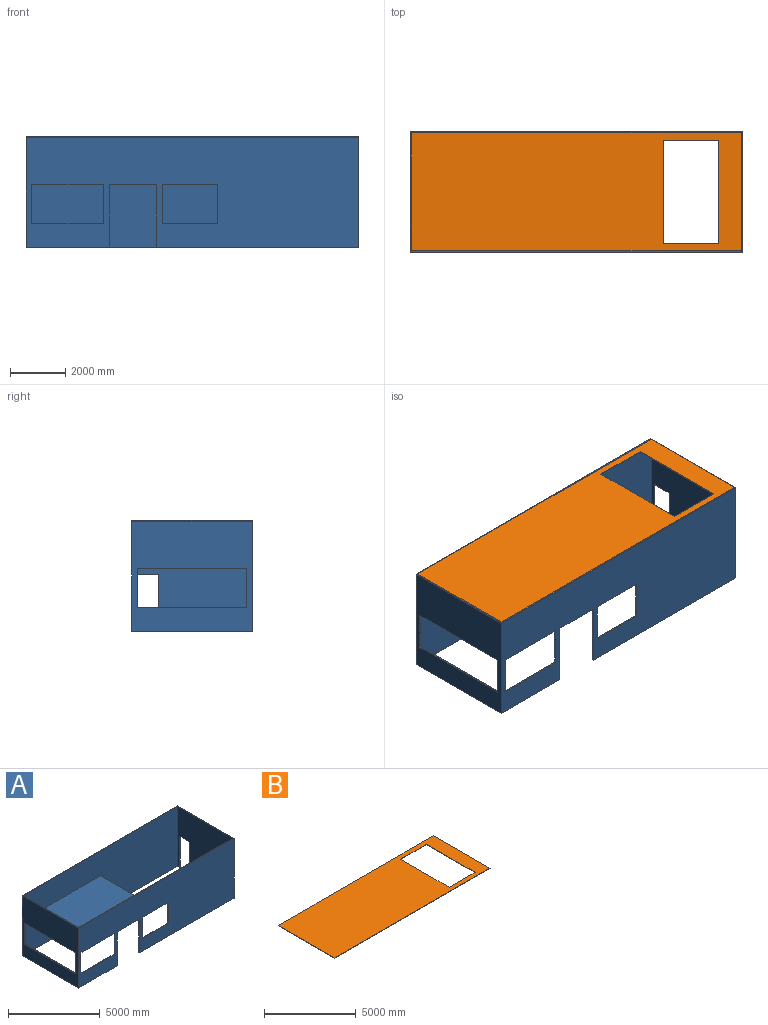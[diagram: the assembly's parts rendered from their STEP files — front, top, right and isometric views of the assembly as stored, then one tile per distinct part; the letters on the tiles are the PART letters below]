
ASSEMBLY  parts=2 mates=1
PART A: 33 faces, bbox 12000x4350x4000 mm
  f0: plane 11925x4000mm, normal (0,1,0), area 36997700mm2, adj f2,f3,f4,f5,f6,f7,f8,f9
  f1: plane 11925x4000mm, normal (0,-1,0), area 47402500mm2, adj f2,f3,f10,f12,f26,f27,f28,f29
  f2: plane 4260x2300mm, normal (1,0,0), area 4208750mm2, adj f0,f1,f10,f21,f22,f23,f25,f28
  f3: plane 4260x1650mm, normal (1,0,0), area 7029000mm2, adj f0,f1,f12,f27
  f4: plane 2600x50mm, normal (0,0,-1), area 130000mm2, adj f0,f5,f19,f20
  f5: plane 1415x50mm, normal (1,0,0), area 70750mm2, adj f0,f4,f6,f20
  f6: plane 2600x50mm, normal (0,0,1), area 130000mm2, adj f0,f5,f19,f20
  f7: plane 2000x50mm, normal (0,0,-1), area 100000mm2, adj f0,f8,f17,f20
  f8: plane 1415x50mm, normal (1,0,0), area 70750mm2, adj f0,f7,f9,f20
  f9: plane 2000x50mm, normal (0,0,1), area 100000mm2, adj f0,f8,f17,f20
  f10: plane 12000x4350mm, normal (0,0,-1), area 847000mm2, adj f0,f1,f2,f11,f13,f18,f20,f24
  f11: plane 4350x4000mm, normal (-1,0,0), area 11810750mm2, adj f10,f12,f20,f21,f22,f23,f24,f25
  f12: plane 12000x4350mm, normal (0,0,1), area 1399500mm2, adj f0,f1,f3,f11,f13,f20,f24,f29
  f13: plane 4350x4000mm, normal (1,0,0), area 15826800mm2, adj f10,f12,f14,f20,f24,f30,f31,f32
  f14: plane 7280x3390mm, normal (0,0,-1), area 447500mm2, adj f0,f13,f15,f20,f29,f30
  f15: plane 2265x50mm, normal (-1,0,0), area 113250mm2, adj f0,f14,f16,f20
  f16: plane 1720x50mm, normal (0,0,-1), area 86000mm2, adj f0,f15,f18,f20
  f17: plane 1415x50mm, normal (-1,0,0), area 70750mm2, adj f0,f7,f9,f20
  f18: plane 2265x50mm, normal (1,0,0), area 113250mm2, adj f0,f10,f16,f20
  f19: plane 1415x50mm, normal (-1,0,0), area 70750mm2, adj f0,f4,f6,f20
  f20: plane 12000x4000mm, normal (0,-1,0), area 37595200mm2, adj f4,f5,f6,f7,f8,f9,f10,f11
  f21: plane 3950x50mm, normal (0,0,-1), area 197500mm2, adj f2,f11,f22,f25
  f22: plane 1415x50mm, normal (0,-1,0), area 70750mm2, adj f2,f11,f21,f23
  f23: plane 3950x50mm, normal (0,0,1), area 197500mm2, adj f2,f11,f22,f25
  f24: plane 12000x4000mm, normal (0,1,0), area 48000000mm2, adj f10,f11,f12,f13
  f25: plane 1415x50mm, normal (0,1,0), area 70750mm2, adj f2,f11,f21,f23
  f26: plane 4260x50mm, normal (1,0,0), area 213000mm2, adj f0,f1,f27,f28
  f27: plane 5950x4260mm, normal (0,0,1), area 25347000mm2, adj f0,f1,f3,f26
  f28: plane 5950x4260mm, normal (0,0,-1), area 25347000mm2, adj f0,f1,f2,f26
  f29: plane 4260x4000mm, normal (-1,0,0), area 15466800mm2, adj f0,f1,f10,f12,f14,f30,f31,f32
  f30: plane 2070x25mm, normal (0,1,0), area 51750mm2, adj f13,f14,f29,f31
  f31: plane 760x25mm, normal (0,0,-1), area 19000mm2, adj f13,f29,f30,f32
  f32: plane 2070x25mm, normal (0,-1,0), area 51750mm2, adj f10,f13,f29,f31
PART B: 10 faces, bbox 12000x4350x25 mm
  f0: plane 3750x25mm, normal (1,0,0), area 93750mm2, adj f1,f7,f8,f9
  f1: plane 2000x25mm, normal (0,-1,0), area 50000mm2, adj f0,f2,f8,f9
  f2: plane 3750x25mm, normal (-1,0,0), area 93750mm2, adj f1,f7,f8,f9
  f3: plane 4350x25mm, normal (-1,0,0), area 108750mm2, adj f4,f6,f8,f9
  f4: plane 12000x25mm, normal (0,-1,0), area 300000mm2, adj f3,f5,f8,f9
  f5: plane 4350x25mm, normal (1,0,0), area 108750mm2, adj f4,f6,f8,f9
  f6: plane 12000x25mm, normal (0,1,0), area 300000mm2, adj f3,f5,f8,f9
  f7: plane 2000x25mm, normal (0,1,0), area 50000mm2, adj f0,f2,f8,f9
  f8: plane 12000x4350mm, normal (0,0,-1), area 44700000mm2, adj f0,f1,f2,f3,f4,f5,f6,f7
  f9: plane 12000x4350mm, normal (0,0,1), area 44700000mm2, adj f0,f1,f2,f3,f4,f5,f6,f7
PLACE A t=(-1502.53,4180.3,2449.11)mm
PLACE B t=(-1502.53,4180.3,2424.11)mm
MATE fastened B.f9 <-> A.f12  axis (0,0,1) through (10497.47,4180.3,6449.11)mm
